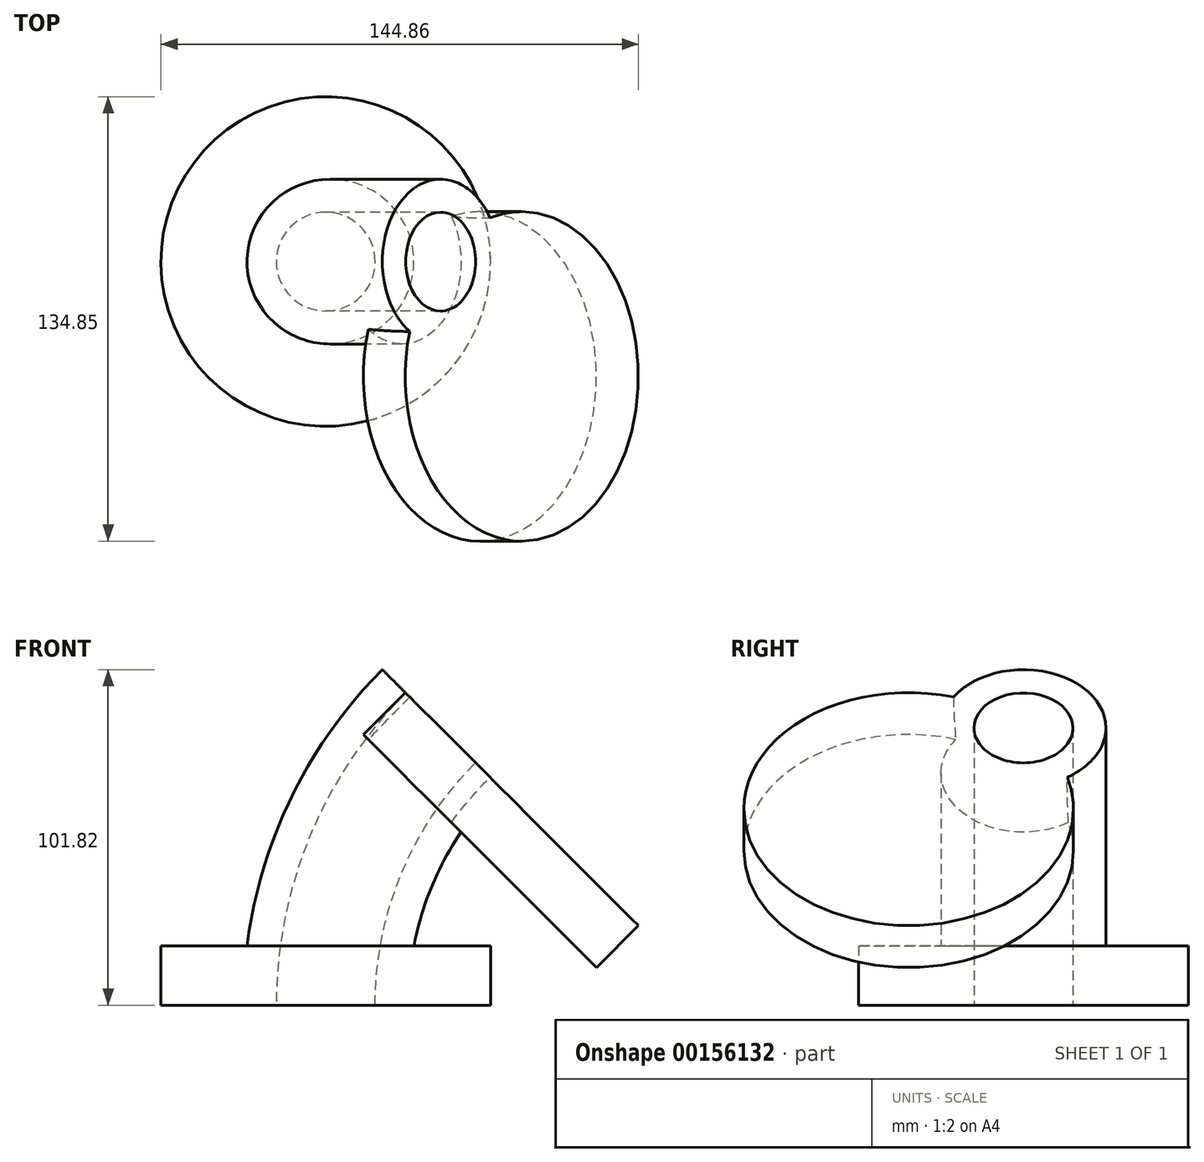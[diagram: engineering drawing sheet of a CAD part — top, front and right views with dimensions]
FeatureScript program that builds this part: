
annotation { "Feature Type Name" : "Feature", "Feature Type Description" : "" }
export const myFeature = defineFeature(function(context is Context, id is Id, definition is map)
    precondition{}
    {
        {
            var Q0;
            Q0=qCreatedBy(makeId("Top.planeOp"),FACE);
            var sketch = newSketch(context, id + "F0", { "sketchPlane" : qUnion([Q0])});
            skCircle(sketch, "E0", {"center": v(0, 0) * mm, "radius": 15 * mm});
            skCircle(sketch, "E1", {"center": v(0, 0) * mm, "radius": 50 * mm});
            skCircle(sketch, "E2", {"center": v(0, 0) * mm, "radius": 25 * mm});
            skSolve(sketch);
        }
        {
            var Q0;
            Q0 = qSketchRegion(id + "F0", true);
            var Q1;
            Q1=makeQuery(id+"F0.imprint","IMPRINT",FACE,{"disambiguationData":[TD([[makeQuery(id+"F0.imprint","IMPRINT",EDGE,{"derivedFrom":sQuery(id+"F0.wireOp",EDGE,"E0")}),-1.0]])]});
            var Q2;
            Q2=makeQuery(id+"F0.imprint","IMPRINT",FACE,{"disambiguationData":[TD([[makeQuery(id+"F0.imprint","IMPRINT",EDGE,{"derivedFrom":sQuery(id+"F0.wireOp",EDGE,"E0")}),1.0]])]});
            extrude(context, id + "F1", {"entities" : qUnion([Q0, Q1, Q2]), "depth" : 18 * mm});
        }
        {
            var Q0;
            Q0=qCreatedBy(makeId("Front.planeOp"),FACE);
            var sketch = newSketch(context, id + "F2", { "sketchPlane" : qUnion([Q0])});
            skLineSegment(sketch, "E3.0", {"start": v(-15, 0) * mm, "end": v(15, 0) * mm});
            skLineSegment(sketch, "E3.1", {"start": v(-25, 0) * mm, "end": v(25, 0) * mm});
            skArc(sketch, "E4", {"start": v(24.25, 94.75) * mm, "mid": v(-4.8, 51.28) * mm, "end": v(-15, 0) * mm});
            skLineSegment(sketch, "E5", {"start": v(24.25, 94.75) * mm, "end": v(119, 0) * mm, "construction": true});
            skSolve(sketch);
        }
        {
            var Q0;
            Q0=makeQuery(id+"F0.imprint","IMPRINT",FACE,{"disambiguationData":[TD([[makeQuery(id+"F0.imprint","IMPRINT",EDGE,{"derivedFrom":sQuery(id+"F0.wireOp",EDGE,"E0")}),1.0]])]});
            var Q1;
            Q1=makeQuery(id+"F0.imprint","IMPRINT",FACE,{"disambiguationData":[TD([[makeQuery(id+"F0.imprint","IMPRINT",EDGE,{"derivedFrom":sQuery(id+"F0.wireOp",EDGE,"E0")}),-1.0]])]});
            var Q2;
            Q2=sQuery(id+"F2.wireOp",EDGE,"E4");
            sweep(context, id + "F3", {"operationType" : NewBodyOperationType.ADD, "profiles" : qUnion([Q0, Q1]), "path" : qUnion([Q2])});
        }
        {
            var Q0;
            Q0=makeQuery(id+"F3.opSweep","CAP_FACE",FACE,{"disambiguationData":[OSD([sQuery(id+"F0.wireOp",EDGE,"E2"),sQuery(id+"F2.wireOp",VERTEX,"E4.start")])],"isStart":false});
            var sketch = newSketch(context, id + "F4", { "sketchPlane" : qUnion([Q0])});
            skCircle(sketch, "E6.0", {"center": v(-34.85, 0) * mm, "radius": 25 * mm});
            skCircle(sketch, "E7", {"center": v(-34.85, 0) * mm, "radius": 50 * mm});
            skSolve(sketch);
        }
        {
            var Q0;
            Q0=makeQuery(id+"F4.imprint","IMPRINT",FACE,{"disambiguationData":[TD([[makeQuery(id+"F4.imprint","IMPRINT",EDGE,{"derivedFrom":sQuery(id+"F4.wireOp",EDGE,"E6.0")}),-1.0]])]});
            var Q1;
            Q1=makeQuery(id+"F4.imprint","IMPRINT",FACE,{"disambiguationData":[TD([[makeQuery(id+"F4.imprint","IMPRINT",EDGE,{"derivedFrom":sQuery(id+"F4.wireOp",EDGE,"E6.0")}),1.0]])]});
            extrude(context, id + "F5", {"entities" : qUnion([Q0, Q1]), "operationType" : NewBodyOperationType.ADD, "oppositeDirection" : true, "depth" : 18 * mm});
        }
        {
            var Q0;
            Q0=makeQuery(id+"F0.imprint","IMPRINT",FACE,{"disambiguationData":[TD([[makeQuery(id+"F0.imprint","IMPRINT",EDGE,{"derivedFrom":sQuery(id+"F0.wireOp",EDGE,"E0")}),1.0]])]});
            var Q1;
            Q1=sQuery(id+"F2.wireOp",EDGE,"E4");
            sweep(context, id + "F6", {"operationType" : NewBodyOperationType.REMOVE, "profiles" : qUnion([Q0]), "path" : qUnion([Q1])});
        }
    });
